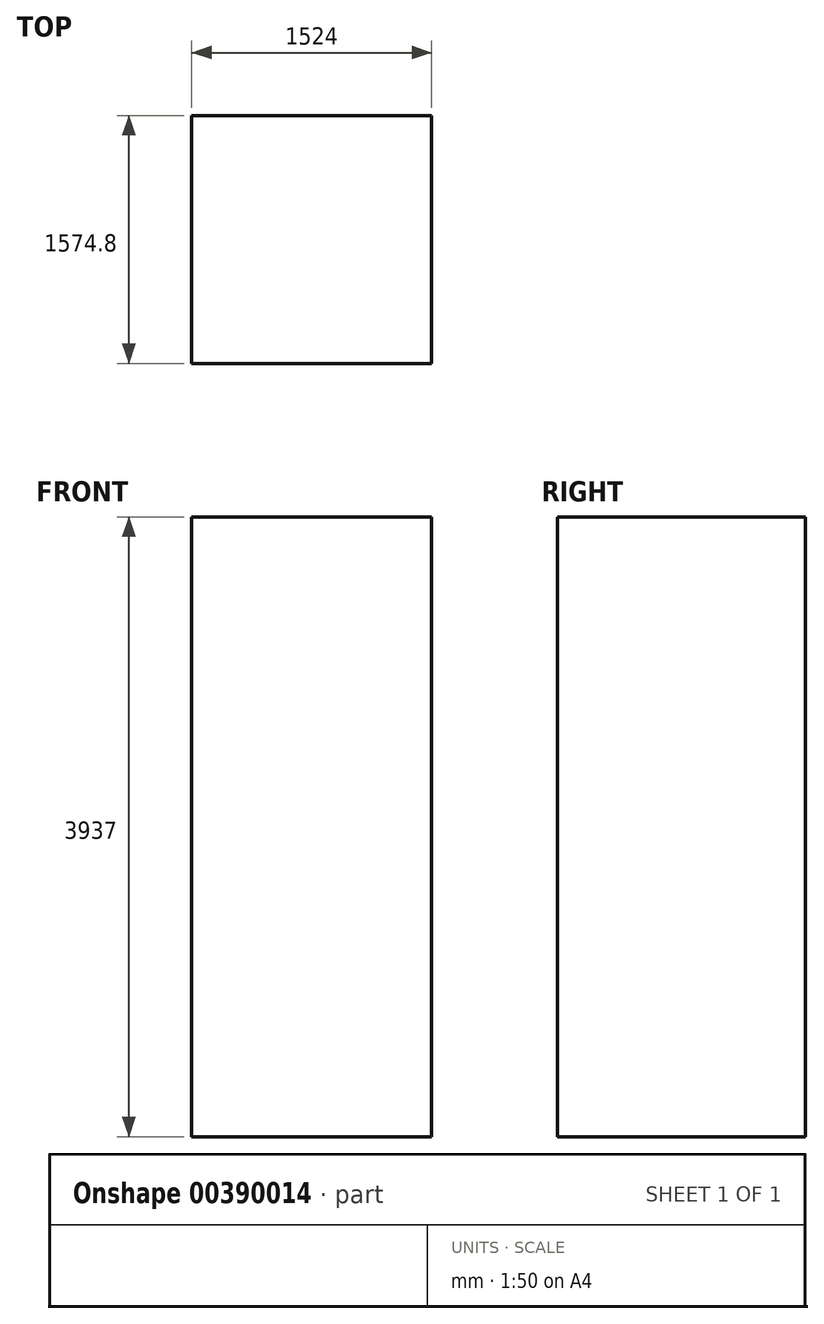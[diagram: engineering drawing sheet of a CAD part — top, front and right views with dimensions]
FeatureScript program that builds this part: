
annotation { "Feature Type Name" : "Feature", "Feature Type Description" : "" }
export const myFeature = defineFeature(function(context is Context, id is Id, definition is map)
    precondition{}
    {
        {
            var Q0;
            Q0=qCreatedBy(makeId("Top.planeOp"),FACE);
            var sketch = newSketch(context, id + "F0", { "sketchPlane" : qUnion([Q0])});
            skLineSegment(sketch, "E0.bottom", {"start": v(762, 787.4) * mm, "end": v(-762, 787.4) * mm});
            skLineSegment(sketch, "E0.top", {"start": v(762, -787.4) * mm, "end": v(-762, -787.4) * mm});
            skLineSegment(sketch, "E0.left", {"start": v(762, 787.4) * mm, "end": v(762, -787.4) * mm});
            skLineSegment(sketch, "E0.right", {"start": v(-762, 787.4) * mm, "end": v(-762, -787.4) * mm});
            skPoint(sketch, "E0.middle", {"position": v(0, 0) * mm});
            skSolve(sketch);
        }
        {
            var Q0;
            Q0 = qSketchRegion(id + "F0", true);
            extrude(context, id + "F1", {"entities" : qUnion([Q0]), "depth" : 3937 * mm});
        }
    });
